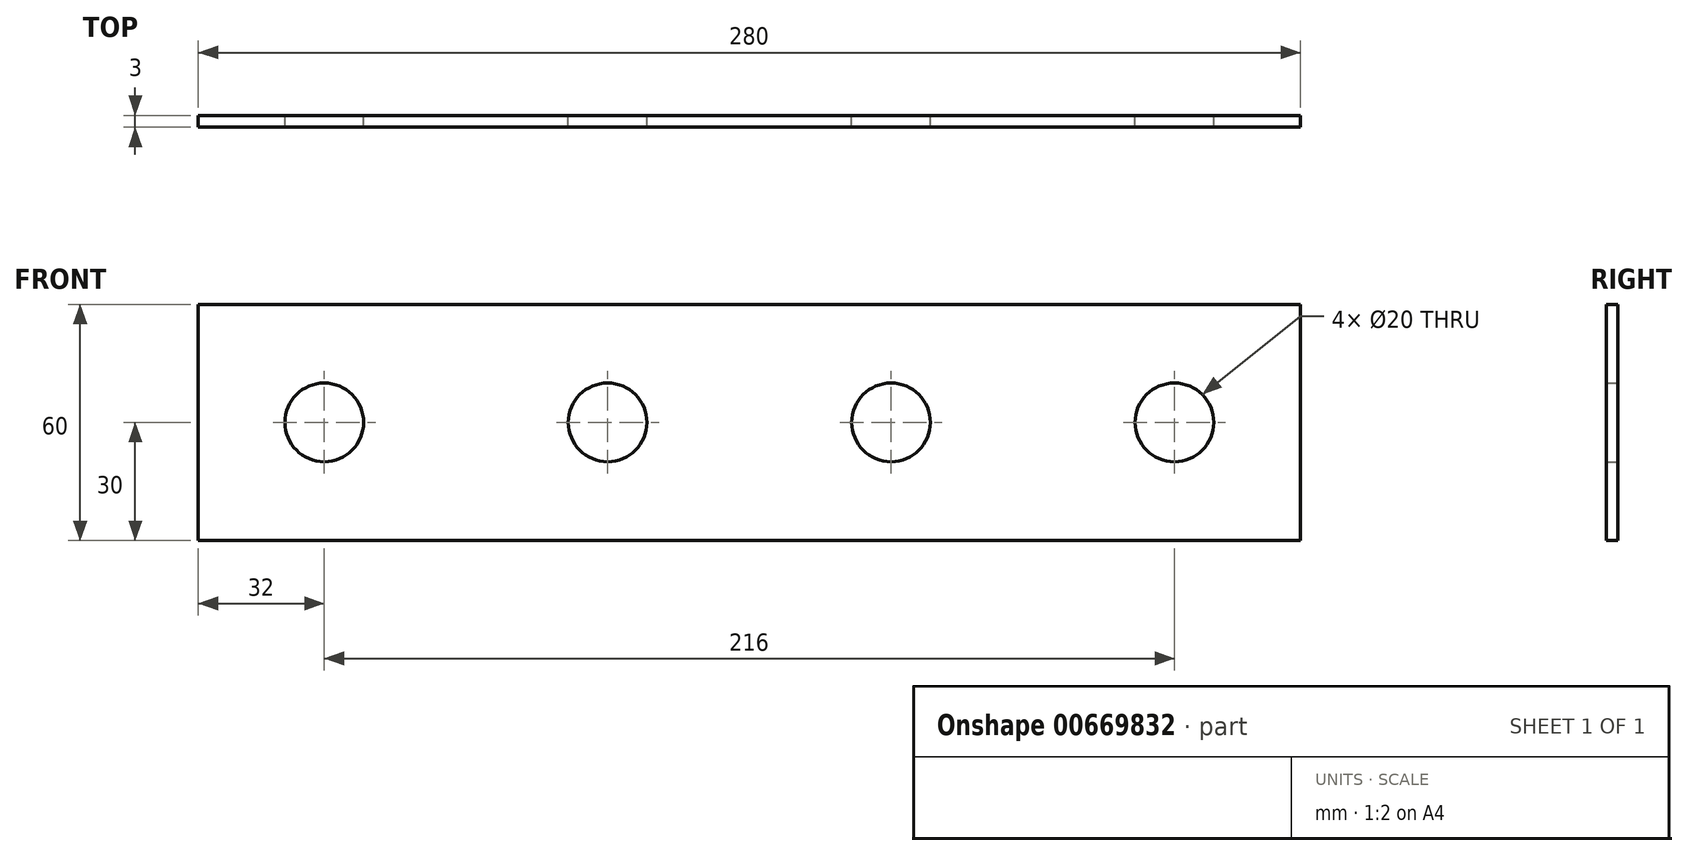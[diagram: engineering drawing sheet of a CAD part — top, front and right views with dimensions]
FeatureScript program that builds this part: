
annotation { "Feature Type Name" : "Feature", "Feature Type Description" : "" }
export const myFeature = defineFeature(function(context is Context, id is Id, definition is map)
    precondition{}
    {
        {
            var Q0;
            Q0=qCreatedBy(makeId("Front.planeOp"),FACE);
            var sketch = newSketch(context, id + "F0", { "sketchPlane" : qUnion([Q0])});
            skLineSegment(sketch, "E0.bottom", {"start": v(-140, 30) * mm, "end": v(140, 30) * mm});
            skLineSegment(sketch, "E0.top", {"start": v(-140, -30) * mm, "end": v(140, -30) * mm});
            skLineSegment(sketch, "E0.left", {"start": v(-140, 30) * mm, "end": v(-140, -30) * mm});
            skLineSegment(sketch, "E0.right", {"start": v(140, 30) * mm, "end": v(140, -30) * mm});
            skPoint(sketch, "E0.middle", {"position": v(0, 0) * mm});
            skLineSegment(sketch, "E1", {"start": v(-36, 0) * mm, "end": v(36, 0) * mm, "construction": true});
            skCircle(sketch, "E2", {"center": v(-36, 0) * mm, "radius": 10 * mm});
            skCircle(sketch, "E3", {"center": v(36, 0) * mm, "radius": 10 * mm});
            skCircle(sketch, "E4", {"center": v(-108, 0) * mm, "radius": 10 * mm});
            skCircle(sketch, "E5", {"center": v(108, 0) * mm, "radius": 10 * mm});
            skLineSegment(sketch, "E6", {"start": v(-36, 0) * mm, "end": v(-108, 0) * mm, "construction": true});
            skLineSegment(sketch, "E7", {"start": v(36, 0) * mm, "end": v(108, 0) * mm, "construction": true});
            skSolve(sketch);
        }
        {
            var Q0;
            Q0=makeQuery(id+"F0.imprint","IMPRINT",FACE,{"disambiguationData":[TD([[makeQuery(id+"F0.imprint","IMPRINT",EDGE,{"derivedFrom":sQuery(id+"F0.wireOp",EDGE,"E0.bottom")}),-1.0]])]});
            extrude(context, id + "F1", {"entities" : qUnion([Q0]), "depth" : 3 * mm, "offsetDistance" : 25 * mm});
        }
    });
